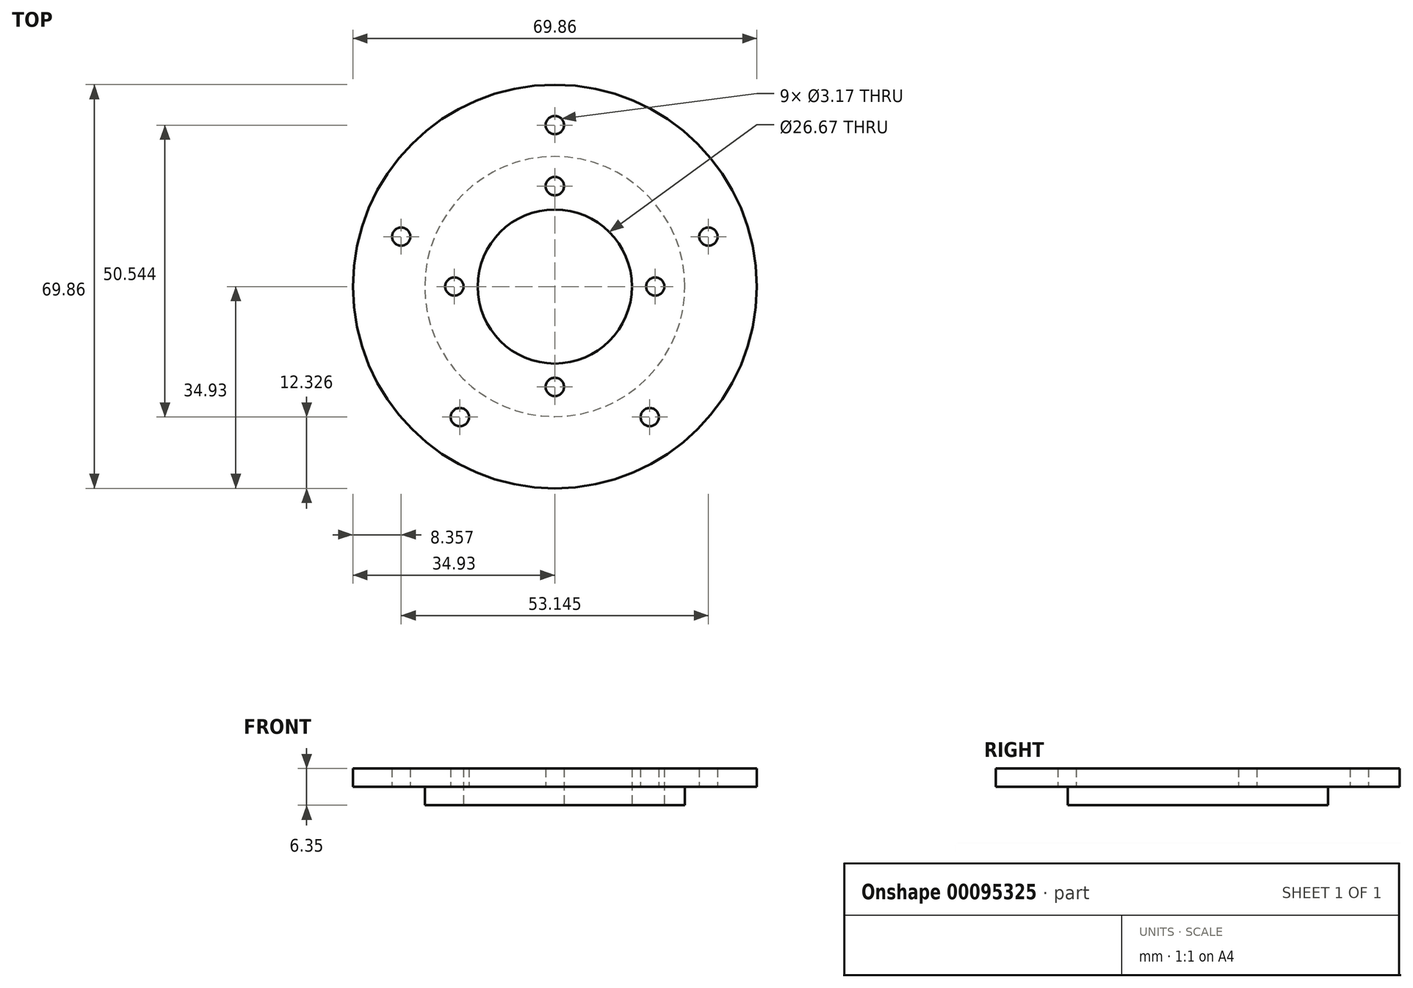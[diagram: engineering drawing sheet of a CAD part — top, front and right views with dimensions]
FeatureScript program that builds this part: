
annotation { "Feature Type Name" : "Feature", "Feature Type Description" : "" }
export const myFeature = defineFeature(function(context is Context, id is Id, definition is map)
    precondition{}
    {
        {
            var Q0;
            Q0=qCreatedBy(makeId("Top.planeOp"),FACE);
            var sketch = newSketch(context, id + "F0", { "sketchPlane" : qUnion([Q0])});
            skCircle(sketch, "E0", {"center": v(0, 0) * mm, "radius": 34.93 * mm});
            skCircle(sketch, "E1", {"center": v(0, 0) * mm, "radius": 13.34 * mm});
            skCircle(sketch, "E2", {"center": v(0, 17.38) * mm, "radius": 1.59 * mm});
            skCircle(sketch, "E3.1.0", {"center": v(-17.38, 0) * mm, "radius": 1.59 * mm});
            skCircle(sketch, "E3.2.0", {"center": v(0, -17.38) * mm, "radius": 1.59 * mm});
            skCircle(sketch, "E3.3.0", {"center": v(17.38, 0) * mm, "radius": 1.59 * mm});
            skCircle(sketch, "E4", {"center": v(0, 27.94) * mm, "radius": 1.59 * mm});
            skCircle(sketch, "E5.1.0", {"center": v(-26.57, 8.63) * mm, "radius": 1.59 * mm});
            skCircle(sketch, "E5.2.0", {"center": v(-16.42, -22.6) * mm, "radius": 1.59 * mm});
            skCircle(sketch, "E5.3.0", {"center": v(16.42, -22.6) * mm, "radius": 1.59 * mm});
            skCircle(sketch, "E5.4.0", {"center": v(26.57, 8.63) * mm, "radius": 1.59 * mm});
            skSolve(sketch);
        }
        {
            var Q0;
            Q0=makeQuery(id+"F0.imprint","IMPRINT",FACE,{"disambiguationData":[TD([[makeQuery(id+"F0.imprint","IMPRINT",EDGE,{"derivedFrom":sQuery(id+"F0.wireOp",EDGE,"E0")}),1.0]])]});
            extrude(context, id + "F1", {"entities" : qUnion([Q0]), "depth" : 6.35 * mm});
        }
        {
            var Q0;
            Q0=makeQuery(id+"F1.opExtrude","CAP_FACE",FACE,{"disambiguationData":[OSD([sQuery(id+"F0.wireOp",EDGE,"E0"),sQuery(id+"F0.wireOp",EDGE,"E1"),sQuery(id+"F0.wireOp",EDGE,"E2"),sQuery(id+"F0.wireOp",EDGE,"E3.1.0"),sQuery(id+"F0.wireOp",EDGE,"E3.2.0"),sQuery(id+"F0.wireOp",EDGE,"E3.3.0")])],"isStart":true});
            var sketch = newSketch(context, id + "F2", { "sketchPlane" : qUnion([Q0])});
            skCircle(sketch, "E6", {"center": v(0, 0) * mm, "radius": 22.5 * mm});
            skCircle(sketch, "E7.0", {"center": v(0, 0) * mm, "radius": 34.93 * mm});
            skSolve(sketch);
        }
        {
            var Q0;
            Q0 = qSketchRegion(id + "F2", true);
            extrude(context, id + "F3", {"entities" : qUnion([Q0]), "operationType" : NewBodyOperationType.REMOVE, "oppositeDirection" : true, "depth" : 3.17 * mm});
        }
    });
